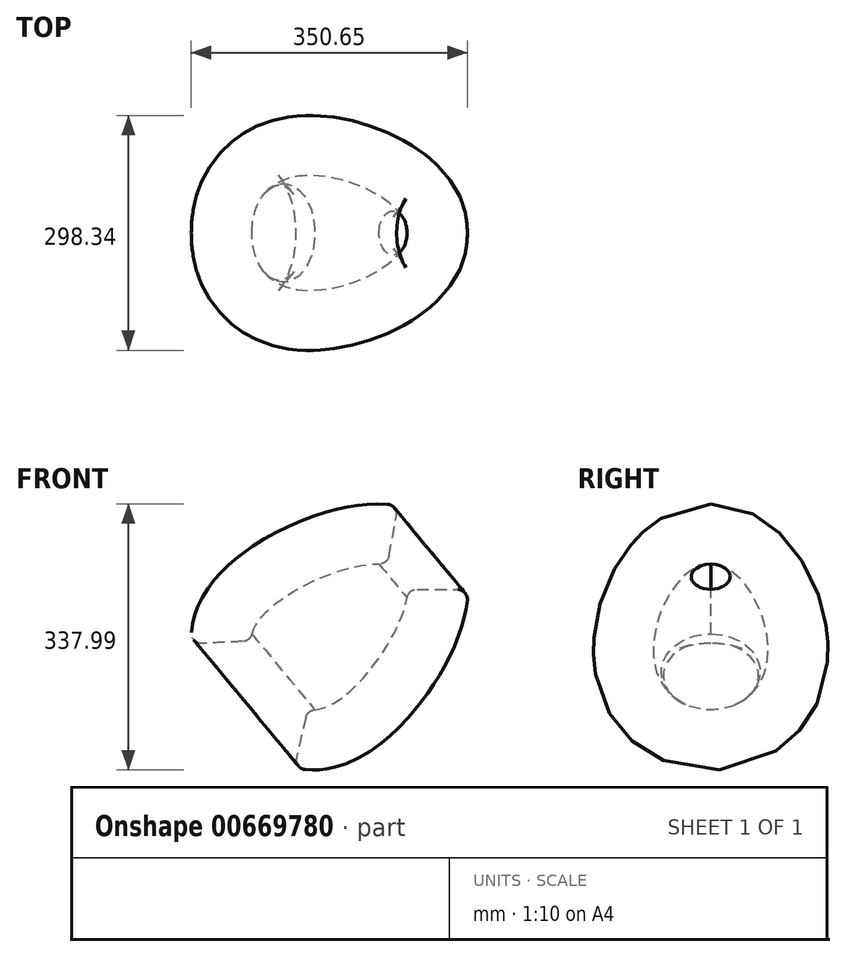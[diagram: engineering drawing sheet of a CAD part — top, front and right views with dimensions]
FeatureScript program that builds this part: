
annotation { "Feature Type Name" : "Feature", "Feature Type Description" : "" }
export const myFeature = defineFeature(function(context is Context, id is Id, definition is map)
    precondition{}
    {
        {
            var Q0;
            Q0=qCreatedBy(makeId("Front.planeOp"),FACE);
            var sketch = newSketch(context, id + "F0", { "sketchPlane" : qUnion([Q0])});
            skFitSpline(sketch, "E0", {"points": [v(-101.34, -20.59) * mm, v(25.66, 131.81) * mm], "startDerivative": vector(136.95, -32.33) * mm, "endDerivative": vector(0, 160.91) * mm});
            skFitSpline(sketch, "E1.0", {"points": [v(-118.84, -94.75) * mm, v(-116.07, -95.4) * mm, v(-110.53, -96.47) * mm, v(-102.37, -97.36) * mm, v(-94.46, -97.62) * mm, v(-86.86, -97.32) * mm, v(-79.6, -96.55) * mm, v(-70.39, -94.98) * mm, v(-59.75, -92.2) * mm, v(-48.24, -87.93) * mm, v(-37.77, -83.01) * mm, v(-28.14, -77.62) * mm, v(-19.17, -71.85) * mm, v(-10.74, -65.74) * mm, v(-2.75, -59.35) * mm, v(4.88, -52.7) * mm, v(14.64, -43.49) * mm, v(26.17, -31.4) * mm, v(39.06, -16.1) * mm, v(51.07, -0.1) * mm, v(62.17, 16.5) * mm, v(72.28, 33.6) * mm, v(79.82, 48.27) * mm, v(85.25, 60.27) * mm, v(89, 69.44) * mm, v(92.4, 78.82) * mm, v(95.43, 88.45) * mm, v(98, 98.43) * mm, v(100.06, 108.86) * mm, v(101.48, 119.87) * mm, v(101.86, 127.73) * mm, v(101.86, 131.81) * mm]});
            skLineSegment(sketch, "E2", {"start": v(-101.34, -20.59) * mm, "end": v(-118.84, -94.75) * mm});
            skLineSegment(sketch, "E3", {"start": v(25.66, 131.81) * mm, "end": v(101.86, 131.81) * mm});
            skLineSegment(sketch, "E4", {"start": v(-239.27, -61.88) * mm, "end": v(61.54, 187.95) * mm});
            skSolve(sketch);
        }
        {
            var Q0;
            Q0=makeQuery(id+"F0.imprint","IMPRINT",FACE,{"disambiguationData":[TD([[makeQuery(id+"F0.imprint","IMPRINT",EDGE,{"derivedFrom":sQuery(id+"F0.wireOp",EDGE,"E0")}),-1.0]])]});
            var Q1;
            Q1=sQuery(id+"F0.wireOp",EDGE,"E4");
            revolve(context, id + "F1", {"entities" : qUnion([Q0]), "axis" : qUnion([Q1]), "revolveType" : RevolveType.FULL});
        }
        {
            var Q0;
            Q0=makeQuery(id+"F1.opRevolve","SWEPT_FACE",FACE,{"disambiguationData":[OSD([sQuery(id+"F0.wireOp",EDGE,"E2")])]});
            var Q1;
            Q1=makeQuery(id+"F1.opRevolve","SWEPT_FACE",FACE,{"disambiguationData":[OSD([sQuery(id+"F0.wireOp",EDGE,"E3")])]});
            var Q2;
            Q2=makeQuery(id+"F1.opRevolve","SWEPT_EDGE",EDGE,{"disambiguationData":[OSD([sQuery(id+"F0.wireOp",EDGE,"E1.0"),sQuery(id+"F0.wireOp",EDGE,"E3")])]});
            fillet(context, id + "F2", {"entities" : qUnion([Q0, Q1, Q2]), "radius" : 12.7 * mm, "tangentPropagation" : true, "allowEdgeOverflow" : false});
        }
    });
